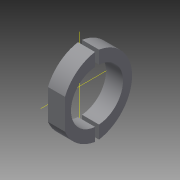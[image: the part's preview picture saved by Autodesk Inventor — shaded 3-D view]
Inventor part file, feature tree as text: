
AUTODESK INVENTOR PART (.ipt)
format: ipt  version: 2015 (Build 190159000, 159)  size: 107,008 bytes
history: native  units: mm
features: extrude x2, sketch x2, projected_geometry x1
ambient origin geometry x8: Origin, YZ Plane, XZ Plane, XY Plane, X Axis, Y Axis, Z Axis, Center Point
bodies: Solid1 (feature_tree)
feature tree (5):
  extrude  "Extrusion1"  Depth=26.0mm
  extrude  "Extrusion2"  Depth=17.0mm
  sketch  "Sketch1"  dims[d2=13.0mm d6=26.0mm]
  sketch  "Sketch5"  dims[d7=9.0mm d9=33.0mm d10=17.0mm d11=0.0mm d13=6.0mm d14=17.0mm d15=0.0mm]
  projected_geometry  "Projected Loop1"
